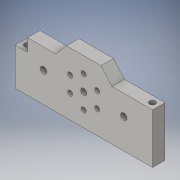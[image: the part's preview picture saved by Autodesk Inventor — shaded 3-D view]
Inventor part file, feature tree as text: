
AUTODESK INVENTOR PART (.ipt)
format: ipt  version: 2016 (Build 200138000, 138)  size: 369,152 bytes
history: native  units: mm
features: projected_geometry x8, extrude x6, other x4, sketch x4, fillet x2, hole x1
ambient origin geometry x8: Origin, YZ Plane, XZ Plane, XY Plane, X Axis, Y Axis, Z Axis, Center Point
bodies: Body1 (feature_tree)
feature tree (25):
  other  "構築線"
  extrude  "押し出し11"  Depth=17.0mm
  other  "固定穴"
  extrude  "押し出し19"  Depth=5.6mm
  extrude  "押し出し21"  Depth=10.0mm
  other  "ねじ穴+固定(基板)"
  hole  "ねじ穴(基板)"  [1 undecoded]
  extrude  "押し出し22"  Depth=10.0mm
  fillet  "フィレット1"  [1 undecoded]
  fillet  "フィレット2"  Radius=20.1mm
  extrude  "押し出し28"  TaperAngle=0.0deg  [1 undecoded]
  other  "外形上面(dxf出力用)"
  sketch  "スケッチ25"
  sketch  "スケッチ27"
  extrude  "押し出し29"  Depth=25.0mm
  sketch  "スケッチ20"
  projected_geometry  "投影ループ4"
  projected_geometry  "投影ループ5"
  projected_geometry  "投影ループ6"
  projected_geometry  "投影ループ7"
  projected_geometry  "投影ループ8"
  projected_geometry  "投影ループ13"
  projected_geometry  "投影ループ14"
  projected_geometry  "投影ループ16"
  sketch  "スケッチ29"
note: 3 required parameter values undecoded (feature->parameter linkage not recoverable at this tier; creation-order binding heuristic only, values carry confidence <= 0.55)
